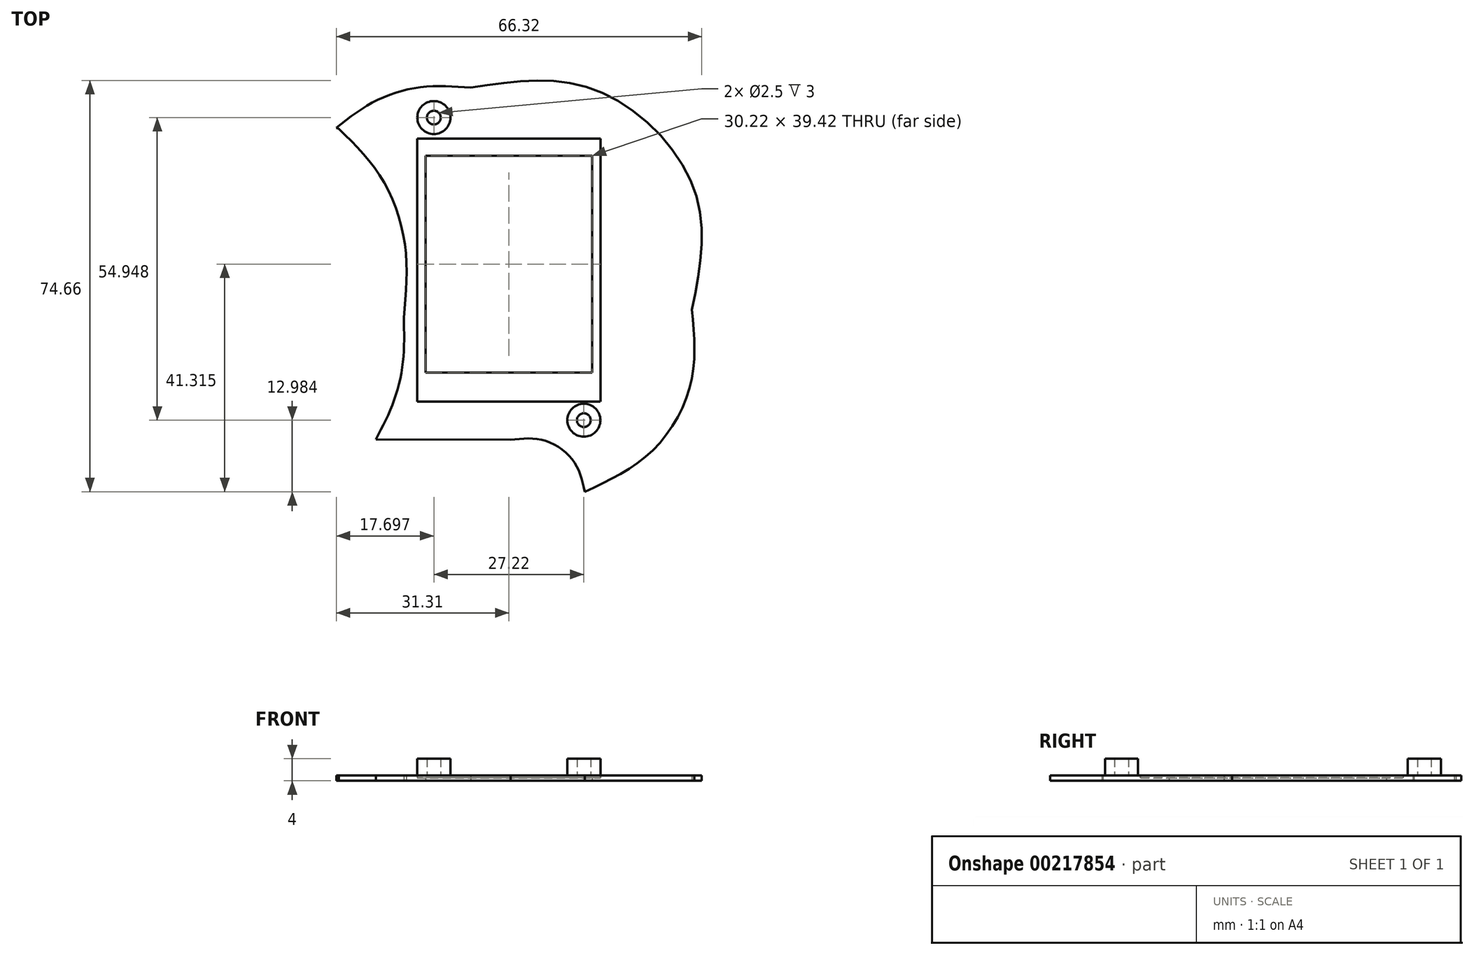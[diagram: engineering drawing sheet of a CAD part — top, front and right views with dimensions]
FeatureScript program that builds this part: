
annotation { "Feature Type Name" : "Feature", "Feature Type Description" : "" }
export const myFeature = defineFeature(function(context is Context, id is Id, definition is map)
    precondition{}
    {
        {
            var Q0;
            Q0=qCreatedBy(makeId("Top.planeOp"),FACE);
            var sketch = newSketch(context, id + "F0", { "sketchPlane" : qUnion([Q0])});
            skFitSpline(sketch, "E0", {"points": [v(12.67, -34.06) * mm, v(24.57, -26.99) * mm, v(31.92, -14.52) * mm, v(32.16, -1) * mm]});
            skFitSpline(sketch, "E1", {"points": [v(32.16, -1) * mm, v(32.55, 20.87) * mm, v(14.56, 38.92) * mm, v(-8.02, 39.3) * mm]});
            skFitSpline(sketch, "E2", {"points": [v(-8.02, 39.3) * mm, v(-16.73, 39.45) * mm, v(-25.28, 36.9) * mm, v(-32.38, 32.02) * mm]});
            skFitSpline(sketch, "E3", {"points": [v(12.7, -34.11) * mm, v(10.67, -28.5) * mm, v(5.3, -24.73) * mm, v(-0.76, -24.62) * mm]});
            skFitSpline(sketch, "E4", {"points": [v(-25.23, -24.54) * mm, v(-22.02, -17.79) * mm, v(-20.26, -10.18) * mm, v(-20.13, -2.44) * mm]});
            skFitSpline(sketch, "E5", {"points": [v(-20.13, -2.44) * mm, v(-19.9, 10.47) * mm, v(-24.17, 22.9) * mm, v(-31.92, 31.83) * mm]});
            skLineSegment(sketch, "E6", {"start": v(-0.76, -24.62) * mm, "end": v(-25.23, -24.54) * mm});
            skLineSegment(sketch, "E7", {"start": v(-17.68, 30.04) * mm, "end": v(15.54, 30.04) * mm});
            skLineSegment(sketch, "E8", {"start": v(15.54, 30.04) * mm, "end": v(15.54, -17.58) * mm});
            skLineSegment(sketch, "E9", {"start": v(15.54, -17.67) * mm, "end": v(-17.68, -17.67) * mm});
            skLineSegment(sketch, "E10", {"start": v(-17.68, -17.58) * mm, "end": v(-17.68, 30.04) * mm});
            skLineSegment(sketch, "E11", {"start": v(-16.18, 26.98) * mm, "end": v(14.04, 26.98) * mm});
            skLineSegment(sketch, "E12", {"start": v(14.04, 26.98) * mm, "end": v(14.04, -13.65) * mm});
            skLineSegment(sketch, "E13", {"start": v(14.04, -12.45) * mm, "end": v(-16.18, -12.45) * mm});
            skLineSegment(sketch, "E14", {"start": v(-16.18, -13.65) * mm, "end": v(-16.18, 26.98) * mm});
            skLineSegment(sketch, "E15", {"start": v(-29.27, 30.49) * mm, "end": v(-28.85, 30.31) * mm});
            skLineSegment(sketch, "E16", {"start": v(-32.38, 32.02) * mm, "end": v(-31.92, 31.83) * mm});
            skLineSegment(sketch, "E17", {"start": v(-17.68, 30.04) * mm, "end": v(-17.68, 33.88) * mm, "construction": true});
            skLineSegment(sketch, "E18", {"start": v(15.54, 30.04) * mm, "end": v(15.54, 33.9) * mm, "construction": true});
            skLineSegment(sketch, "E19", {"start": v(12.53, 36.9) * mm, "end": v(-14.69, 36.88) * mm, "construction": true});
            skLineSegment(sketch, "E20.top", {"start": v(-14.68, -24.07) * mm, "end": v(12.54, -24.07) * mm, "construction": true});
            skLineSegment(sketch, "E20.left", {"start": v(-17.68, -17.67) * mm, "end": v(-17.68, -21.07) * mm, "construction": true});
            skLineSegment(sketch, "E20.right", {"start": v(15.54, -17.67) * mm, "end": v(15.54, -21.07) * mm, "construction": true});
            skPoint(sketch, "E21.visualSharp", {"position": v(-17.68, -24.07) * mm});
            skArc(sketch, "E21.filletArc", {"start": v(-17.68, -21.07) * mm, "mid": v(-16.8, -23.19) * mm, "end": v(-14.68, -24.07) * mm, "construction": true});
            skPoint(sketch, "E22.visualSharp", {"position": v(15.54, -24.07) * mm});
            skArc(sketch, "E22.filletArc", {"start": v(12.54, -24.07) * mm, "mid": v(14.66, -23.19) * mm, "end": v(15.54, -21.07) * mm, "construction": true});
            skPoint(sketch, "E23.visualSharp", {"position": v(-17.68, 36.88) * mm});
            skArc(sketch, "E23.filletArc", {"start": v(-14.69, 36.88) * mm, "mid": v(-16.8, 36) * mm, "end": v(-17.68, 33.88) * mm, "construction": true});
            skPoint(sketch, "E24.visualSharp", {"position": v(15.54, 36.91) * mm});
            skArc(sketch, "E24.filletArc", {"start": v(15.54, 33.9) * mm, "mid": v(14.66, 36.03) * mm, "end": v(12.53, 36.9) * mm, "construction": true});
            skCircle(sketch, "E25", {"center": v(-14.68, 33.88) * mm, "radius": 3 * mm});
            skCircle(sketch, "E26", {"center": v(-14.68, 33.88) * mm, "radius": 1.25 * mm});
            skCircle(sketch, "E27", {"center": v(12.54, -21.07) * mm, "radius": 3 * mm});
            skCircle(sketch, "E28", {"center": v(12.54, -21.07) * mm, "radius": 1.25 * mm});
            skLineSegment(sketch, "E29", {"start": v(-17.68, -17.58) * mm, "end": v(-17.68, -17.67) * mm});
            skLineSegment(sketch, "E30", {"start": v(15.54, -17.58) * mm, "end": v(15.54, -17.67) * mm});
            skSolve(sketch);
        }
        {
            var Q0;
            Q0=makeQuery(id+"F0.imprint","IMPRINT",FACE,{"disambiguationData":[TD([[makeQuery(id+"F0.imprint","IMPRINT",EDGE,{"derivedFrom":sQuery(id+"F0.wireOp",EDGE,"E25")}),1.0]])]});
            var Q1;
            Q1=makeQuery(id+"F0.imprint","IMPRINT",FACE,{"disambiguationData":[TD([[makeQuery(id+"F0.imprint","IMPRINT",EDGE,{"derivedFrom":sQuery(id+"F0.wireOp",EDGE,"E27")}),1.0]])]});
            var Q2;
            {var subQ0=sQuery(id+"F0.wireOp",EDGE,"E1");Q2=makeQuery(id+"F0.imprint","IMPRINT",FACE,{"disambiguationData":[TD([[makeQuery(id+"F0.imprint","IMPRINT",EDGE,{"derivedFrom":subQ0}),1.0]])]});}
            var Q3;
            Q3=makeQuery(id+"F0.imprint","IMPRINT",FACE,{"disambiguationData":[TD([[makeQuery(id+"F0.imprint","IMPRINT",EDGE,{"derivedFrom":sQuery(id+"F0.wireOp",EDGE,"E26")}),1.0]])]});
            var Q4;
            Q4=makeQuery(id+"F0.imprint","IMPRINT",FACE,{"disambiguationData":[TD([[makeQuery(id+"F0.imprint","IMPRINT",EDGE,{"derivedFrom":sQuery(id+"F0.wireOp",EDGE,"E28")}),1.0]])]});
            extrude(context, id + "F1", {"entities" : qUnion([Q0, Q1, Q2, Q3, Q4]), "depth" : 1 * mm});
        }
        {
            var Q0;
            Q0=makeQuery(id+"F0.imprint","IMPRINT",FACE,{"disambiguationData":[TD([[makeQuery(id+"F0.imprint","IMPRINT",EDGE,{"derivedFrom":sQuery(id+"F0.wireOp",EDGE,"E7")}),-1.0]])]});
            extrude(context, id + "F2", {"entities" : qUnion([Q0]), "operationType" : NewBodyOperationType.ADD, "depth" : 0.5 * mm});
        }
        {
            var Q0;
            Q0=makeQuery(id+"F0.imprint","IMPRINT",FACE,{"disambiguationData":[TD([[makeQuery(id+"F0.imprint","IMPRINT",EDGE,{"derivedFrom":sQuery(id+"F0.wireOp",EDGE,"E27")}),1.0]])]});
            var Q1;
            Q1=makeQuery(id+"F0.imprint","IMPRINT",FACE,{"disambiguationData":[TD([[makeQuery(id+"F0.imprint","IMPRINT",EDGE,{"derivedFrom":sQuery(id+"F0.wireOp",EDGE,"E26")}),-1.0]])]});
            extrude(context, id + "F3", {"entities" : qUnion([Q0, Q1]), "operationType" : NewBodyOperationType.ADD, "depth" : 4 * mm});
        }
    });
